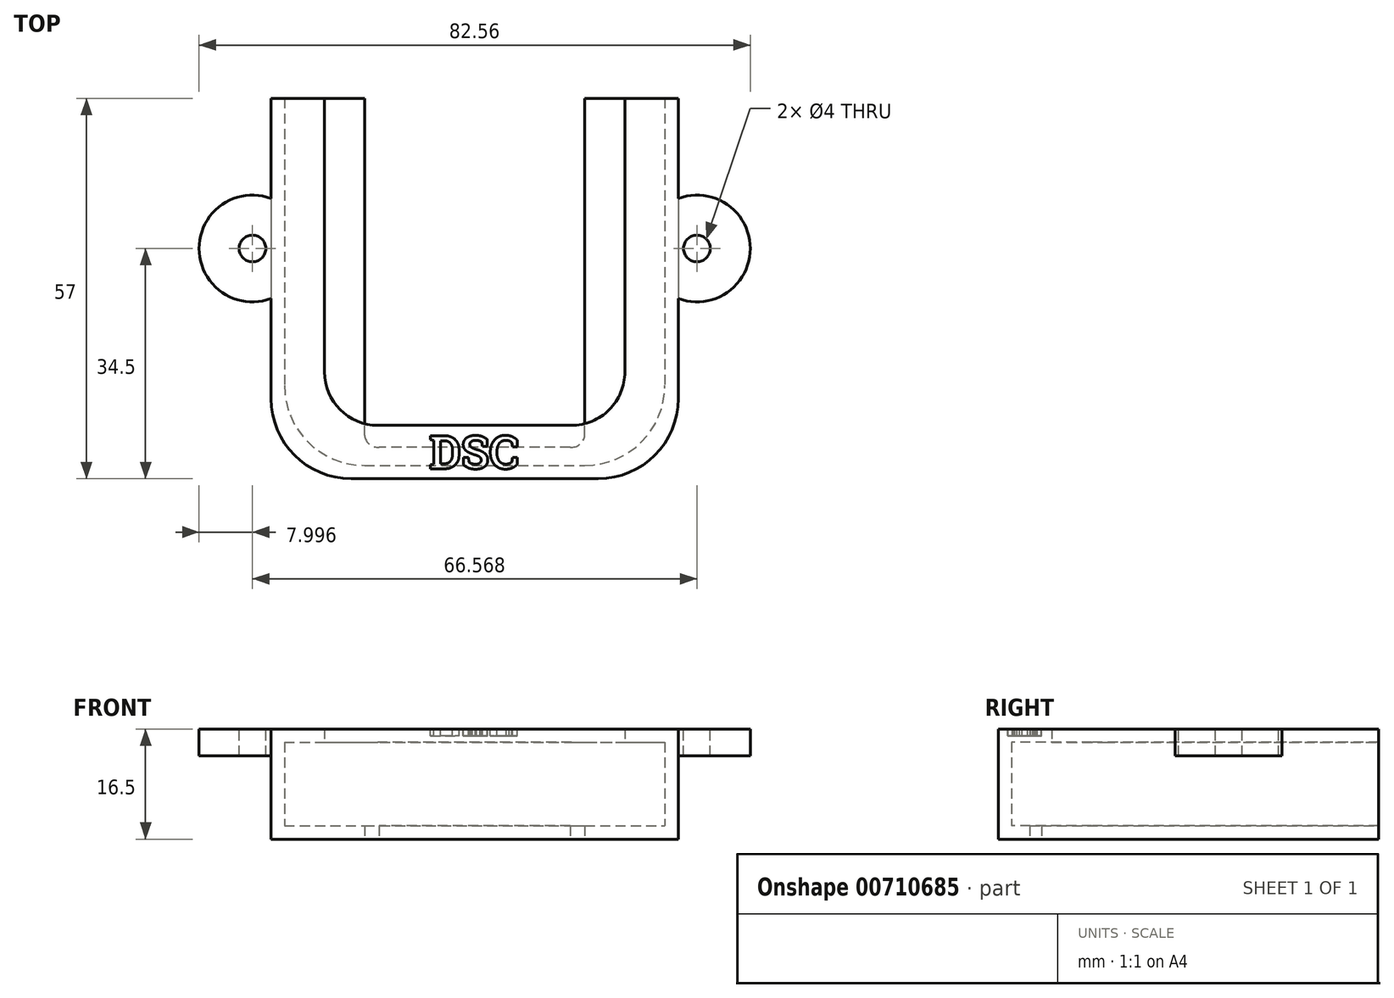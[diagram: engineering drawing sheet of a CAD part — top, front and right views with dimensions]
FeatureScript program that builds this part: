
annotation { "Feature Type Name" : "Feature", "Feature Type Description" : "" }
export const myFeature = defineFeature(function(context is Context, id is Id, definition is map)
    precondition{}
    {
        {
            var Q0;
            Q0=qCreatedBy(makeId("Top.planeOp"),FACE);
            var sketch = newSketch(context, id + "F0", { "sketchPlane" : qUnion([Q0])});
            skLineSegment(sketch, "E0.top", {"start": v(-18.5, -34.5) * mm, "end": v(18.5, -34.5) * mm});
            skLineSegment(sketch, "E0.left", {"start": v(-30.5, 22.5) * mm, "end": v(-30.5, -22.5) * mm});
            skLineSegment(sketch, "E0.right", {"start": v(30.5, 22.5) * mm, "end": v(30.5, -22.5) * mm});
            skPoint(sketch, "E1.visualSharp", {"position": v(-30.5, 34.5) * mm});
            skPoint(sketch, "E2.visualSharp", {"position": v(30.5, 34.5) * mm});
            skPoint(sketch, "E3.visualSharp", {"position": v(-30.5, -34.5) * mm});
            skArc(sketch, "E3.filletArc", {"start": v(-30.5, -22.5) * mm, "mid": v(-26.99, -30.99) * mm, "end": v(-18.5, -34.5) * mm});
            skPoint(sketch, "E4.visualSharp", {"position": v(30.5, -34.5) * mm});
            skArc(sketch, "E4.filletArc", {"start": v(18.5, -34.5) * mm, "mid": v(26.99, -30.99) * mm, "end": v(30.5, -22.5) * mm});
            skPoint(sketch, "E5", {"position": v(-24.99, 30.99) * mm});
            skPoint(sketch, "E6", {"position": v(26.99, -30.99) * mm});
            skLineSegment(sketch, "E7", {"start": v(-30.5, 22.5) * mm, "end": v(30.5, 22.5) * mm});
            skSolve(sketch);
        }
        {
            var Q0;
            Q0=makeQuery(id+"F0.imprint","IMPRINT",FACE,{"disambiguationData":[TD([[makeQuery(id+"F0.imprint","IMPRINT",EDGE,{"derivedFrom":sQuery(id+"F0.wireOp",EDGE,"E0.top")}),1.0]])]});
            extrude(context, id + "F1", {"entities" : qUnion([Q0]), "depth" : 16.5 * mm, "offsetDistance" : 25 * mm});
        }
        {
            var Q0;
            Q0=qCreatedBy(makeId("Top.planeOp"),FACE);
            var sketch = newSketch(context, id + "F2", { "sketchPlane" : qUnion([Q0])});
            skLineSegment(sketch, "E8.top", {"start": v(-16.5, 68.04) * mm, "end": v(16.5, 68.04) * mm});
            skLineSegment(sketch, "E8.left", {"start": v(-28.5, 125.04) * mm, "end": v(-28.5, 80.04) * mm});
            skLineSegment(sketch, "E8.right", {"start": v(28.5, 125.04) * mm, "end": v(28.5, 80.04) * mm});
            skPoint(sketch, "E9.visualSharp", {"position": v(-28.5, 137.04) * mm});
            skPoint(sketch, "E10.visualSharp", {"position": v(28.5, 137.04) * mm});
            skPoint(sketch, "E11.visualSharp", {"position": v(-28.5, 68.04) * mm});
            skArc(sketch, "E11.filletArc", {"start": v(-28.5, 80.04) * mm, "mid": v(-24.99, 71.55) * mm, "end": v(-16.5, 68.04) * mm});
            skPoint(sketch, "E12.visualSharp", {"position": v(28.5, 68.04) * mm});
            skArc(sketch, "E12.filletArc", {"start": v(16.5, 68.04) * mm, "mid": v(24.99, 71.55) * mm, "end": v(28.5, 80.04) * mm});
            skPoint(sketch, "E13", {"position": v(-28.86, 133.52) * mm});
            skPoint(sketch, "E14", {"position": v(24.99, 71.55) * mm});
            skLineSegment(sketch, "E15", {"start": v(-28.5, 125.04) * mm, "end": v(28.5, 125.04) * mm});
            skSolve(sketch);
        }
        {
            var Q0;
            Q0=makeQuery(id+"F2.imprint","IMPRINT",FACE,{"disambiguationData":[TD([[makeQuery(id+"F2.imprint","IMPRINT",EDGE,{"derivedFrom":sQuery(id+"F2.wireOp",EDGE,"E8.top")}),1.0]])]});
            extrude(context, id + "F3", {"entities" : qUnion([Q0]), "depth" : 12.5 * mm, "offsetDistance" : 25 * mm});
        }
        {
            var Q0;
            Q0=makeQuery(id+"F3.opExtrude","SWEPT_BODY",BODY,{"disambiguationData":[OSD([sQuery(id+"F2.wireOp",EDGE,"E8.top"),sQuery(id+"F2.wireOp",EDGE,"E8.left"),sQuery(id+"F2.wireOp",EDGE,"E8.right"),sQuery(id+"F2.wireOp",EDGE,"E11.filletArc"),sQuery(id+"F2.wireOp",EDGE,"E12.filletArc"),sQuery(id+"F2.wireOp",EDGE,"E15")])]});
            transform(context, id + "F4", {"entities" : qUnion([Q0]), "transformType" : TransformType.TRANSLATION_3D, "dx" : 0 * mm, "dy" : 0 * mm, "dz" : 2 * mm, "makeCopy" : false});
        }
        {
            var Q0;
            Q0=makeQuery(id+"F3.opExtrude","SWEPT_BODY",BODY,{"disambiguationData":[OSD([sQuery(id+"F2.wireOp",EDGE,"E8.top"),sQuery(id+"F2.wireOp",EDGE,"E8.left"),sQuery(id+"F2.wireOp",EDGE,"E8.right"),sQuery(id+"F2.wireOp",EDGE,"E11.filletArc"),sQuery(id+"F2.wireOp",EDGE,"E12.filletArc"),sQuery(id+"F2.wireOp",EDGE,"E15")])]});
            transform(context, id + "F5", {"entities" : qUnion([Q0]), "transformType" : TransformType.TRANSLATION_3D, "dx" : 0 * mm, "dy" : -100.54 * mm, "dz" : 0 * mm, "makeCopy" : false});
        }
        {
            var Q0;
            Q0=makeQuery(id+"F3.opExtrude","SWEPT_BODY",BODY,{"disambiguationData":[OSD([sQuery(id+"F2.wireOp",EDGE,"E8.top"),sQuery(id+"F2.wireOp",EDGE,"E8.left"),sQuery(id+"F2.wireOp",EDGE,"E8.right"),sQuery(id+"F2.wireOp",EDGE,"E11.filletArc"),sQuery(id+"F2.wireOp",EDGE,"E12.filletArc"),sQuery(id+"F2.wireOp",EDGE,"E15")])]});
            var Q1;
            Q1=makeQuery(id+"F1.opExtrude","SWEPT_BODY",BODY,{"disambiguationData":[OSD([sQuery(id+"F0.wireOp",EDGE,"E0.top"),sQuery(id+"F0.wireOp",EDGE,"E0.left"),sQuery(id+"F0.wireOp",EDGE,"E0.right"),sQuery(id+"F0.wireOp",EDGE,"E3.filletArc"),sQuery(id+"F0.wireOp",EDGE,"E4.filletArc"),sQuery(id+"F0.wireOp",EDGE,"E7")])]});
            booleanBodies(context, id + "F6", {"operationType" : BooleanOperationType.SUBTRACTION, "tools" : qUnion([Q0]), "targets" : qUnion([Q1])});
        }
        {
            var Q0;
            Q0=makeQuery(id+"F1.opExtrude","CAP_FACE",FACE,{"disambiguationData":[OSD([sQuery(id+"F0.wireOp",EDGE,"E0.top"),sQuery(id+"F0.wireOp",EDGE,"E0.left"),sQuery(id+"F0.wireOp",EDGE,"E0.right"),sQuery(id+"F0.wireOp",EDGE,"E3.filletArc"),sQuery(id+"F0.wireOp",EDGE,"E4.filletArc"),sQuery(id+"F0.wireOp",EDGE,"E7")])],"isStart":false});
            var sketch = newSketch(context, id + "F7", { "sketchPlane" : qUnion([Q0])});
            skLineSegment(sketch, "E16.top", {"start": v(-14.5, 105.03) * mm, "end": v(14.5, 105.03) * mm});
            skLineSegment(sketch, "E16.left", {"start": v(-22.5, 166.36) * mm, "end": v(-22.5, 113.03) * mm});
            skLineSegment(sketch, "E16.right", {"start": v(22.5, 166.36) * mm, "end": v(22.5, 113.03) * mm});
            skPoint(sketch, "E17.visualSharp", {"position": v(-28.5, 101.03) * mm});
            skArc(sketch, "E17.filletArc", {"start": v(-22.5, 113.03) * mm, "mid": v(-20.16, 107.38) * mm, "end": v(-14.5, 105.03) * mm});
            skPoint(sketch, "E18.visualSharp", {"position": v(28.5, 101.03) * mm});
            skArc(sketch, "E18.filletArc", {"start": v(14.5, 105.03) * mm, "mid": v(20.16, 107.38) * mm, "end": v(22.5, 113.03) * mm});
            skLineSegment(sketch, "E19", {"start": v(-22.5, 166.36) * mm, "end": v(22.5, 166.36) * mm});
            skArc(sketch, "E20", {"start": v(30.5, -7.5) * mm, "mid": v(41.28, 0) * mm, "end": v(30.5, 7.5) * mm});
            skArc(sketch, "E21", {"start": v(-30.5, 7.5) * mm, "mid": v(-41.28, 0) * mm, "end": v(-30.5, -7.5) * mm});
            skSolve(sketch);
        }
        {
            var Q0;
            Q0=makeQuery(id+"F7.imprint","IMPRINT",FACE,{"disambiguationData":[TD([[makeQuery(id+"F7.imprint","IMPRINT",EDGE,{"derivedFrom":sQuery(id+"F7.wireOp",EDGE,"E16.top")}),1.0]])]});
            extrude(context, id + "F8", {"entities" : qUnion([Q0]), "endBound" : BoundingType.SYMMETRIC, "depth" : 5 * mm, "offsetDistance" : 25 * mm});
        }
        {
            var Q0;
            Q0=makeQuery(id+"F8.opExtrude","SWEPT_BODY",BODY,{"disambiguationData":[OSD([sQuery(id+"F7.wireOp",EDGE,"E16.top"),sQuery(id+"F7.wireOp",EDGE,"E16.left"),sQuery(id+"F7.wireOp",EDGE,"E16.right"),sQuery(id+"F7.wireOp",EDGE,"E17.filletArc"),sQuery(id+"F7.wireOp",EDGE,"E18.filletArc"),sQuery(id+"F7.wireOp",EDGE,"E19")])]});
            transform(context, id + "F9", {"entities" : qUnion([Q0]), "transformType" : TransformType.TRANSLATION_3D, "dx" : 0 * mm, "dy" : -131.53 * mm, "dz" : 0 * mm, "makeCopy" : false});
        }
        {
            var Q0;
            Q0=makeQuery(id+"F8.opExtrude","SWEPT_BODY",BODY,{"disambiguationData":[OSD([sQuery(id+"F7.wireOp",EDGE,"E16.top"),sQuery(id+"F7.wireOp",EDGE,"E16.left"),sQuery(id+"F7.wireOp",EDGE,"E16.right"),sQuery(id+"F7.wireOp",EDGE,"E17.filletArc"),sQuery(id+"F7.wireOp",EDGE,"E18.filletArc"),sQuery(id+"F7.wireOp",EDGE,"E19")])]});
            var Q1;
            Q1=makeQuery(id+"F1.opExtrude","SWEPT_BODY",BODY,{"disambiguationData":[OSD([sQuery(id+"F0.wireOp",EDGE,"E0.top"),sQuery(id+"F0.wireOp",EDGE,"E0.left"),sQuery(id+"F0.wireOp",EDGE,"E0.right"),sQuery(id+"F0.wireOp",EDGE,"E3.filletArc"),sQuery(id+"F0.wireOp",EDGE,"E4.filletArc"),sQuery(id+"F0.wireOp",EDGE,"E7")])]});
            booleanBodies(context, id + "F10", {"operationType" : BooleanOperationType.SUBTRACTION, "tools" : qUnion([Q0]), "targets" : qUnion([Q1])});
        }
        {
            var Q0;
            Q0=qCreatedBy(makeId("Top.planeOp"),FACE);
            var sketch = newSketch(context, id + "F11", { "sketchPlane" : qUnion([Q0])});
            skLineSegment(sketch, "E22.top", {"start": v(-14.32, 71.23) * mm, "end": v(14.32, 71.23) * mm});
            skLineSegment(sketch, "E22.left", {"start": v(-16.5, 142.25) * mm, "end": v(-16.5, 72.97) * mm});
            skLineSegment(sketch, "E22.right", {"start": v(16.5, 142.25) * mm, "end": v(16.5, 72.97) * mm});
            skArc(sketch, "E23.filletArc", {"start": v(-16.5, 72.97) * mm, "mid": v(-15.76, 71.65) * mm, "end": v(-14.32, 71.23) * mm});
            skArc(sketch, "E24.filletArc", {"start": v(14.32, 71.23) * mm, "mid": v(15.76, 71.65) * mm, "end": v(16.5, 72.97) * mm});
            skLineSegment(sketch, "E25", {"start": v(-16.5, 142.25) * mm, "end": v(16.5, 142.25) * mm});
            skSolve(sketch);
        }
        {
            var Q0;
            Q0=makeQuery(id+"F11.imprint","IMPRINT",FACE,{"disambiguationData":[TD([[makeQuery(id+"F11.imprint","IMPRINT",EDGE,{"derivedFrom":sQuery(id+"F11.wireOp",EDGE,"E22.top")}),1.0]])]});
            extrude(context, id + "F12", {"entities" : qUnion([Q0]), "endBound" : BoundingType.SYMMETRIC, "depth" : 6 * mm, "offsetDistance" : 25 * mm});
        }
        {
            var Q0;
            Q0=makeQuery(id+"F12.opExtrude","SWEPT_BODY",BODY,{"disambiguationData":[OSD([sQuery(id+"F11.wireOp",EDGE,"E22.top"),sQuery(id+"F11.wireOp",EDGE,"E22.left"),sQuery(id+"F11.wireOp",EDGE,"E22.right"),sQuery(id+"F11.wireOp",EDGE,"E23.filletArc"),sQuery(id+"F11.wireOp",EDGE,"E24.filletArc"),sQuery(id+"F11.wireOp",EDGE,"E25")])]});
            transform(context, id + "F13", {"entities" : qUnion([Q0]), "transformType" : TransformType.TRANSLATION_3D, "dx" : 0 * mm, "dy" : -101 * mm, "dz" : 0 * mm, "makeCopy" : false});
        }
        {
            var Q0;
            Q0=makeQuery(id+"F12.opExtrude","SWEPT_BODY",BODY,{"disambiguationData":[OSD([sQuery(id+"F11.wireOp",EDGE,"E22.top"),sQuery(id+"F11.wireOp",EDGE,"E22.left"),sQuery(id+"F11.wireOp",EDGE,"E22.right"),sQuery(id+"F11.wireOp",EDGE,"E23.filletArc"),sQuery(id+"F11.wireOp",EDGE,"E24.filletArc"),sQuery(id+"F11.wireOp",EDGE,"E25")])]});
            var Q1;
            Q1=makeQuery(id+"F1.opExtrude","SWEPT_BODY",BODY,{"disambiguationData":[OSD([sQuery(id+"F0.wireOp",EDGE,"E0.top"),sQuery(id+"F0.wireOp",EDGE,"E0.left"),sQuery(id+"F0.wireOp",EDGE,"E0.right"),sQuery(id+"F0.wireOp",EDGE,"E3.filletArc"),sQuery(id+"F0.wireOp",EDGE,"E4.filletArc"),sQuery(id+"F0.wireOp",EDGE,"E7")])]});
            booleanBodies(context, id + "F14", {"operationType" : BooleanOperationType.SUBTRACTION, "tools" : qUnion([Q0]), "targets" : qUnion([Q1])});
        }
        {
            var Q0;
            Q0=makeQuery(id+"F1.opExtrude","CAP_FACE",FACE,{"disambiguationData":[OSD([sQuery(id+"F0.wireOp",EDGE,"E0.top"),sQuery(id+"F0.wireOp",EDGE,"E0.left"),sQuery(id+"F0.wireOp",EDGE,"E0.right"),sQuery(id+"F0.wireOp",EDGE,"E3.filletArc"),sQuery(id+"F0.wireOp",EDGE,"E4.filletArc"),sQuery(id+"F0.wireOp",EDGE,"E7")])],"isStart":false});
            var sketch = newSketch(context, id + "F15", { "sketchPlane" : qUnion([Q0])});
            skText(sketch, "E26", { "text": "DSC", "fontName": "RobotoSlab-Bold.ttf"});
            const initialGuessF15  = {"E26": [-0.00683, -0.033, 1, 0, 0.005]};
            skSetInitialGuess(sketch, initialGuessF15);
            skSolve(sketch);
        }
        {
            var Q0;
            Q0 = qSketchRegion(id + "F15", true);
            extrude(context, id + "F16", {"entities" : qUnion([Q0]), "operationType" : NewBodyOperationType.REMOVE, "oppositeDirection" : true, "depth" : 1 * mm, "offsetDistance" : 25 * mm});
        }
        {
            var Q0;
            {var subQ0=sQuery(id+"F7.wireOp",EDGE,"E20");Q0=makeQuery(id+"F7.imprint","IMPRINT",FACE,{"disambiguationData":[TD([[makeQuery(id+"F7.imprint","IMPRINT",EDGE,{"derivedFrom":subQ0}),1.0]])]});}
            var Q1;
            {var subQ0=sQuery(id+"F7.wireOp",EDGE,"E21");Q1=makeQuery(id+"F7.imprint","IMPRINT",FACE,{"disambiguationData":[TD([[makeQuery(id+"F7.imprint","IMPRINT",EDGE,{"derivedFrom":subQ0}),1.0]])]});}
            extrude(context, id + "F17", {"entities" : qUnion([Q0, Q1]), "operationType" : NewBodyOperationType.ADD, "oppositeDirection" : true, "depth" : 4 * mm, "offsetDistance" : 25 * mm});
        }
        {
            var Q0;
            Q0=sQuery(id+"F7.wireOp",VERTEX,"E21.center");
            var Q1;
            Q1=sQuery(id+"F7.wireOp",VERTEX,"E20.center");
            var Q2;
            Q2=makeQuery(id+"F16.boolean.opBoolean","SPLIT",BODY,{"disambiguationData":[OD(0.0)],"derivedFrom":makeQuery(id+"F1.opExtrude","SWEPT_BODY",BODY,{"disambiguationData":[OSD([sQuery(id+"F0.wireOp",EDGE,"E0.top"),sQuery(id+"F0.wireOp",EDGE,"E0.left"),sQuery(id+"F0.wireOp",EDGE,"E0.right"),sQuery(id+"F0.wireOp",EDGE,"E3.filletArc"),sQuery(id+"F0.wireOp",EDGE,"E4.filletArc"),sQuery(id+"F0.wireOp",EDGE,"E7")])]})});
            hole(context, id + "F18", {"style" : HoleStyle.SIMPLE, "endStyle" : HoleEndStyle.BLIND, "holeDiameter" : 4 * mm, "majorDiameter" : 5 * mm, "holeDepth" : 8 * mm, "isTappedThrough" : true, "tappedDepth" : 12 * mm, "tapClearance" : 3, "startFromSketch" : true, "locations" : qUnion([Q0, Q1]), "scope" : qUnion([Q2])});
        }
    });
